# Revit family: HourdiBox PP Néo 150 Up 23 KW-1
name_source: partatom
category: Equipement spécialisé
revit_build: Autodesk Revit Structure 2016 (Build: 20150220_1215(x64)
units: mm (PartAtom-declared; Revit-internal decimal feet)

## family parameters
Basée sur le plan de construction = Non
Couper avec des vides une fois chargée = Non
Partagée = Non
Point de calcul de pièce = Non
Toujours verticalement = Oui

## types (1)
- HourdiBox PP 150 Up 23
    Coût = 0 $
    Epaisseur de languette = 101 mm  [stored 0.331365 ft]
    Fabricant = Isobox
    Largeur = 689 mm
    Longueur = 1200 mm
    Matériaux = Isolant PSE Entrevous
    Modèle = Entrevous 120 - UP 14
    Rp - DURANDAL DF 110 - DURANDAL DF 130 - DURANDAL DF 140 = 4.2000 (m²·K)/W
    Rp - KP1 Leader 110 - KP1 Leader 115S - KP1 Leader x 110 = 4.3000 (m²·K)/W
    Rp - KP1 Leader 130 - KP1 Leader 140 = 4.2000 (m²·K)/W
    Rp - LB 7 - Série 2 = 4.2000 (m²·K)/W
    Rp - LB7 - Série 1 = 4.2500 (m²·K)/W
    Rp - RECTOR NR 110 = 4.2500 (m²·K)/W
    Rp - RECTOR NR 130 = 4.1500 (m²·K)/W
    Rp - SEAC GF 110 - SEAC GF 120 - SEAC GF 930 - SEAC GF 940 = 4.2000 (m²·K)/W
    URL = http://www.isobox-isolation.fr
    Up - DURANDAL DF 110 - DURANDAL DF 130 - DURANDAL DF 140 = 0.2200 W/(m·K)
    Up - KP1 Leader 110 - KP1 Leader 115S - KP1 Leader x 110 = 0.2200 W/(m·K)
    Up - KP1 Leader 130 - KP1 Leader 140 = 0.2200 W/(m·K)
    Up - LB 7 - Série 2 = 0.2200 W/(m·K)
    Up - LB7 - Série 1 = 0.2200 W/(m·K)
    Up - RECTOR NR 110 = 0.2200 W/(m·K)
    Up - RECTOR NR 130 = 0.2200 W/(m·K)
    Up - SEAC GF 110 - SEAC GF 120 - SEAC GF 930 - SEAC GF 940 = 0.2200 W/(m·K)

note: [stored X ft] marks values corroborated as IEEE doubles in the binary element streams (Revit-internal decimal feet)
